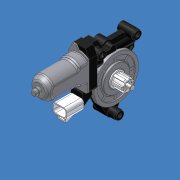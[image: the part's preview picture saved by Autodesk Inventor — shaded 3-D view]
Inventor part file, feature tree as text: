
AUTODESK INVENTOR PART (.ipt)
format: ipt  version: 2012 (Build 160160000, 160)  size: 1,677,824 bytes
history: native  units: mm (DEFAULTED — no unit token found)
features: sketch x59, extrude x51, fillet x11, chamfer x9, hole x6, pattern_circular x4, revolve x2, plane x2, other x1, mirror x1, projected_geometry x1
ambient origin geometry x8: Origin, YZ Plane, XZ Plane, XY Plane, X Axis, Y Axis, Z Axis, Center Point
bodies: Solid1 (feature_tree)
feature tree (147):
  extrude  "Extrusion1"  Depth=5.0mm TaperAngle=0.0deg
  extrude  "Extrusion2"  Depth=42.0mm
  extrude  "Extrusion3"  Depth=2.0mm
  extrude  "Extrusion4"  Depth=26.0mm
  extrude  "Extrusion5"  Depth=4.0mm
  pattern_circular  "Circular Pattern1"  Count=8 Angle=360.0deg
  extrude  "Extrusion6"  Depth=1.7mm TaperAngle=0.0deg
  extrude  "Extrusion7"  Depth=17.9mm TaperAngle=0.0deg
  hole  "Hole1"  [1 undecoded]
  extrude  "Extrusion8"  Depth=18.0mm TaperAngle=0.0deg
  chamfer  "Chamfer1"  Distance=2.0mm
  pattern_circular  "Circular Pattern2"  Count=6 Angle=360.0deg
  extrude  "Extrusion9"  Depth=0.2mm TaperAngle=0.0deg
  extrude  "Extrusion10"  Depth=8.2mm TaperAngle=0.0deg
  chamfer  "Chamfer2"  Distance=0.5mm
  fillet  "Fillet1"  Radius=0.5mm
  fillet  "Fillet2"  Radius=1.5mm
  extrude  "Extrusion11"  Depth=0.5mm TaperAngle=0.0deg
  extrude  "Extrusion12"  Depth=68.0mm
  extrude  "Extrusion13"  Depth=2.0mm
  revolve  "Revolution1"  [1 undecoded]
  extrude  "Extrusion14"  TaperAngle=30.0deg  [1 undecoded]
  pattern_circular  "Circular Pattern3"  Count=12 Angle=360.0deg
  extrude  "Extrusion15"  Depth=0.5mm
  fillet  "Fillet3"  Radius=43.0mm
  extrude  "Extrusion16"  Depth=2.0mm TaperAngle=0.0deg
  fillet  "Fillet4"  Radius=1.0mm
  hole  "Hole2"  [1 undecoded]
  extrude  "Extrusion18"  Depth=0.9mm
  fillet  "Fillet5"  Radius=120.0mm
  pattern_circular  "Circular Pattern4"  Count=2  [1 undecoded]
  plane  "Work Plane1"
  plane  "Work Plane2"
  other  "Work Axis1"
  extrude  "Extrusion19"  Depth=23.0mm
  extrude  "Extrusion20"  Depth=5.0mm TaperAngle=0.0deg
  extrude  "Extrusion21"  Depth=31.0mm
  extrude  "Extrusion22"  Depth=4.0mm
  extrude  "Extrusion23"  Depth=6.0mm
  fillet  "Fillet6"  Radius=0.2mm
  chamfer  "Chamfer3"  Distance=2.0mm
  chamfer  "Chamfer4"  Distance=15.0mm
  extrude  "Extrusion24"  Depth=17.5mm
  fillet  "Fillet7"  Radius=40.0mm
  extrude  "Extrusion25"  Depth=1.0mm
  extrude  "Extrusion26"  TaperAngle=90.0deg  [1 undecoded]
  chamfer  "Chamfer5"  Distance=43.0mm
  chamfer  "Chamfer6"  Distance=4.0mm
  fillet  "Fillet8"  Radius=9.0mm
  revolve  "Revolution2"  [1 undecoded]
  extrude  "Extrusion27"  Depth=2.0mm TaperAngle=0.0deg
  mirror  "Mirror1"
  fillet  "Fillet9"  Radius=13.2mm
  extrude  "Extrusion28"  Depth=18.0mm TaperAngle=0.0deg
  extrude  "Extrusion29"  Depth=7.0mm
  fillet  "Fillet10"  Radius=50.0mm
  extrude  "Extrusion30"  Depth=14.0mm
  extrude  "Extrusion31"  Depth=8.2mm TaperAngle=0.0deg
  chamfer  "Chamfer8"  Distance=3.0mm
  extrude  "Extrusion32"  Depth=22.68928mm
  extrude  "Extrusion33"  Depth=2.0mm TaperAngle=0.0deg
  extrude  "Extrusion34"  Depth=56.58mm
  hole  "Hole3"  [1 undecoded]
  extrude  "Extrusion35"  Depth=8.0mm TaperAngle=0.0deg
  extrude  "Extrusion36"  Depth=15.5mm
  extrude  "Extrusion39"  Depth=5.0mm
  extrude  "Extrusion40"  Depth=41.0mm
  extrude  "Extrusion41"  Depth=16.0mm TaperAngle=0.0deg
  hole  "Hole4"  [1 undecoded]
  extrude  "Extrusion42"  Depth=3.5mm
  extrude  "Extrusion43"  Depth=6.25mm
  extrude  "Extrusion46"  Depth=9.5mm TaperAngle=0.0deg
  extrude  "Extrusion47"  Depth=14.2mm
  extrude  "Extrusion48"  Depth=48.4mm
  hole  "Hole5"  [1 undecoded]
  hole  "Hole6"  [1 undecoded]
  extrude  "Extrusion50"  Depth=3.0mm TaperAngle=0.0deg
  extrude  "Extrusion51"  Depth=16.5mm
  extrude  "Extrusion52"  Depth=17.5mm TaperAngle=0.0deg
  extrude  "Extrusion53"  Depth=2.0mm TaperAngle=0.0deg
  chamfer  "Chamfer9"  Distance=2.0mm
  extrude  "Extrusion55"  Depth=13.0mm TaperAngle=0.0deg
  fillet  "Fillet12"  Radius=18.5mm
  extrude  "Extrusion56"  Depth=9.0mm
  extrude  "Extrusion57"  Depth=2.0mm
  chamfer  "Chamfer10"  Distance=15.0mm
  extrude  "Extrusion59"  Depth=19.0mm
  sketch  "Sketch1"  dims[d0=72.0mm d1=5.0mm d2=0.0mm]
  sketch  "Sketch2"  dims[d3=60.0mm d4=42.0mm]
  sketch  "Sketch3"  dims[d5=2.0mm d6=0.0mm d7=2.0mm]
  sketch  "Sketch4"  dims[d8=1.0mm d9=0.0mm d10=26.0mm]
  sketch  "Sketch5"  dims[d11=0.5mm d12=0.0mm d13=4.0mm]
  sketch  "Sketch6"  dims[d14=8.0mm]
  sketch  "Sketch7"  dims[d15=22.0mm]
  sketch  "Sketch8"  dims[d16=1.5mm d17=0.0mm]
  sketch  "Sketch9"  dims[d18=2.0mm d19=80.0mm d21=360.0deg]
  sketch  "Sketch10"  dims[d22=23.9mm d23=1.7mm d24=0.0mm]
  sketch  "Sketch11"  dims[d25=16.2mm d26=17.9mm d27=0.0mm]
  sketch  "Sketch12"  dims[d28=13.0mm d29=6.0mm d30=4.0mm d31=2.0mm d32=14.3117mm d33=2.0mm d34=0.0mm d35=4.0mm]
  sketch  "Sketch13"  dims[d36=10.0mm d37=18.0mm d38=0.0mm d39=2.0mm d40=2.0mm d41=60.0mm d43=360.0deg]
  sketch  "Sketch14"  dims[d44=12.5mm d45=0.2mm d46=0.0mm]
  sketch  "Sketch15"  dims[d47=8.0mm d48=8.2mm d49=0.0mm d50=0.5mm d51=2.0mm d52=0.5mm d53=1.5mm]
  sketch  "Sketch16"  dims[d54=71.0mm d55=0.5mm d56=0.0mm]
  sketch  "Sketch17"  dims[d57=3.0mm d58=0.0mm d59=68.0mm]
  sketch  "Sketch18"  dims[d60=14.0mm d61=0.0mm d62=2.0mm]
  sketch  "Sketch19"  dims[d63=3.5mm d64=10.0mm]
  sketch  "Sketch21"  dims[d65=90.0deg d66=30.0deg]
  sketch  "Sketch22"  dims[d67=1.0mm]
  sketch  "Sketch23"  dims[d68=1.0mm]
  sketch  "Sketch24"  dims[d69=4.5mm d70=0.0mm d71=120.0mm d73=360.0deg]
  sketch  "Sketch25"  dims[d74=0.5mm d75=0.0mm d76=0.5mm d77=43.0mm]
  sketch  "Sketch26"  dims[d78=2.0mm d79=2.0mm d80=0.0mm d81=1.0mm]
  sketch  "Sketch27"  dims[d82=2.6mm d83=6.0mm d84=4.0mm d85=2.0mm d86=14.3117mm d87=8.0mm d88=0.0mm d93=2.0mm]
  sketch  "Sketch28"  dims[d94=15.5mm d95=0.0mm d96=0.9mm d97=120.0mm d99=360.0deg]
  sketch  "Sketch29"  dims[d100=-12.0mm d101=-33.88mm]
  sketch  "Sketch30"  dims[d102=15.0mm]
  projected_geometry  "Projected Loop1"
  sketch  "Sketch31"  dims[d103=35.0mm d104=0.0mm d105=20.0mm d106=0.0mm]
  sketch  "Sketch32"  dims[d108=14.5mm d109=0.0mm d110=23.0mm]
  sketch  "Sketch33"  dims[d111=12.25mm d112=5.0mm d113=0.0mm]
  sketch  "Sketch35"  dims[d114=60.0mm d115=31.0mm]
  sketch  "Sketch36"  dims[d116=12.5mm d117=0.0mm d118=4.0mm]
  sketch  "Sketch37"  dims[d119=12.0mm d120=6.0mm d121=6.0mm d122=12.0mm d123=0.2mm]
  sketch  "Sketch38"  dims[d124=0.2mm]
  sketch  "Sketch39"  dims[d125=0.2mm]
  sketch  "Sketch40"  dims[d126=120.0deg d127=2.0mm d128=0.0mm]
  sketch  "Sketch41"  dims[d129=1.0mm]
  sketch  "Sketch43"  dims[d130=40.0mm d131=15.0mm d132=0.0mm]
  sketch  "Sketch46"  dims[d133=35.0mm d134=17.5mm d135=40.0mm d136=0.0mm]
  sketch  "Sketch47"  dims[d137=2.5mm d138=12.0mm d139=1.0mm d140=12.0mm]
  sketch  "Sketch48"  dims[d143=4.0mm d144=90.0deg d145=43.0mm d146=0.0mm]
  sketch  "Sketch49"  dims[d147=8.0mm]
  sketch  "Sketch50"  dims[d148=12.0mm]
  sketch  "Sketch51"  dims[d149=4.0mm]
  sketch  "Sketch54"  dims[d150=10.0mm d151=4.0mm d152=0.0mm d153=9.0mm]
  sketch  "Sketch55"  dims[d154=5.0mm d155=0.0mm d156=1.0mm]
  sketch  "Sketch56"  dims[d157=0.5mm d158=2.0mm d159=0.0mm d160=13.2mm]
  sketch  "Sketch57"  dims[d161=30.0mm d162=18.0mm d163=0.0mm]
  sketch  "Sketch58"  dims[d164=9.0mm d165=14.0mm d166=7.0mm d167=50.0mm d168=0.0mm]
  sketch  "Sketch60"  dims[d169=14.88mm d170=14.0mm]
  sketch  "Sketch61"  dims[d171=20.71mm d172=8.2mm d173=0.0mm]
  sketch  "Sketch63"  dims[d174=12.3mm d175=3.0mm d176=0.0mm]
  sketch  "Sketch66"  dims[d177=4.8mm d178=6.0mm d179=6.2mm d180=2.0mm d181=14.3117mm d182=8.0mm d183=0.0mm d184=22.68928mm]
  sketch  "Sketch68"  dims[d185=4.0mm d186=2.0mm d187=0.0mm]
  sketch  "Sketch69"  dims[d191=7.0mm d192=0.0mm d199=56.58mm]
  sketch  "Sketch70"  dims[d200=14.8mm d201=0.0mm d202=12.3mm]
  sketch  "Sketch72"  dims[d203=3.0mm d204=0.0mm d205=8.0mm d206=0.0mm d207=4.8mm d208=6.0mm d209=6.2mm d210=2.0mm d211=14.3117mm d212=8.0mm d213=0.0mm d214=15.5mm d215=5.0mm d216=41.0mm d217=16.0mm d218=0.0mm d219=9.0mm d220=3.5mm d221=6.25mm d222=9.5mm d223=0.0mm d230=14.2mm d231=48.4mm d232=14.8mm d233=0.0mm d234=12.3mm d235=3.0mm d236=0.0mm d237=16.5mm d238=17.5mm d239=0.0mm d240=4.8mm d241=6.0mm d242=6.2mm d243=2.0mm d244=14.3117mm d245=28.0mm d246=20.594885mm d247=4.134mm d248=6.0mm d249=4.9mm d250=2.0mm d251=14.3117mm d252=8.0mm d253=0.0mm d259=2.0mm d260=0.0mm d261=2.0mm d262=0.0mm d263=13.0mm d264=0.0mm d270=18.5mm d271=0.0mm d272=9.0mm d273=13.0mm d280=2.0mm d281=15.0mm d282=19.0mm d284=23.0mm d285=15.5mm d286=7.5mm d287=27.3mm d288=0.0mm d289=5.0mm d290=1.6mm d291=24.3mm d292=0.0mm d293=13.8mm d294=3.0mm d295=7.0mm d296=0.0mm d302=5.0mm d303=10.0mm d304=9.0mm d305=2.0mm d306=12.5mm d307=0.0mm d308=20.0mm d309=2.0mm d310=2.0mm d311=45.0deg d312=45.0deg d313=45.0deg d314=45.0deg d315=45.0deg d316=45.0deg d317=45.0deg d318=45.0deg d319=45.0deg]
note: 11 required parameter values undecoded (feature->parameter linkage not recoverable at this tier; creation-order binding heuristic only, values carry confidence <= 0.55)